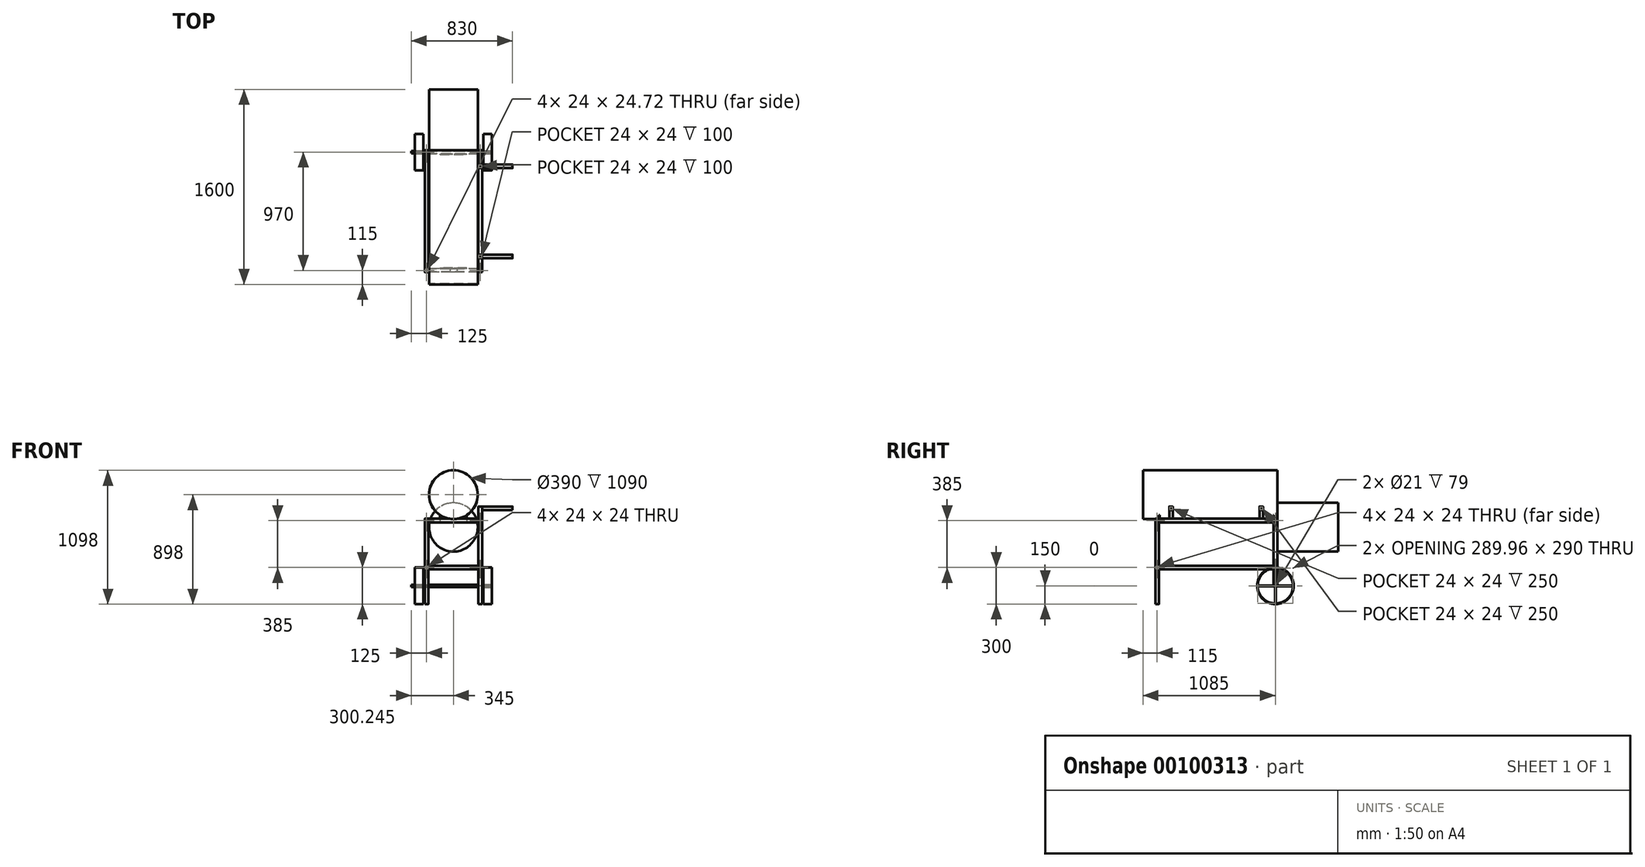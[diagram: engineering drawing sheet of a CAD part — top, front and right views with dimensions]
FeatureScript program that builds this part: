
annotation { "Feature Type Name" : "Feature", "Feature Type Description" : "" }
export const myFeature = defineFeature(function(context is Context, id is Id, definition is map)
    precondition{}
    {
        {
            var Q0;
            Q0=qCreatedBy(makeId("Front.planeOp"),FACE);
            var sketch = newSketch(context, id + "F0", { "sketchPlane" : qUnion([Q0])});
            skLineSegment(sketch, "E0.bottom", {"start": v(15, -350) * mm, "end": v(-15, -350) * mm});
            skLineSegment(sketch, "E0.top", {"start": v(15, 350) * mm, "end": v(-15, 350) * mm});
            skLineSegment(sketch, "E0.left", {"start": v(15, -350) * mm, "end": v(15, 350) * mm});
            skLineSegment(sketch, "E0.right", {"start": v(-15, -350) * mm, "end": v(-15, 350) * mm});
            skPoint(sketch, "E0.middle", {"position": v(0, 0) * mm});
            skSolve(sketch);
        }
        {
            var Q0;
            Q0=makeQuery(id+"F0.imprint","IMPRINT",FACE,{"disambiguationData":[TD([[makeQuery(id+"F0.imprint","IMPRINT",EDGE,{"derivedFrom":sQuery(id+"F0.wireOp",EDGE,"E0.bottom")}),-1.0]])]});
            extrude(context, id + "F1", {"entities" : qUnion([Q0]), "endBound" : BoundingType.SYMMETRIC, "oppositeDirection" : true, "depth" : 30 * mm});
        }
        {
            var Q0;
            Q0=makeQuery(id+"F1.opExtrude","SWEPT_FACE",FACE,{"disambiguationData":[OSD([sQuery(id+"F0.wireOp",EDGE,"E0.bottom")])]});
            var sketch = newSketch(context, id + "F2", { "sketchPlane" : qUnion([Q0])});
            skLineSegment(sketch, "E1.bottom", {"start": v(12, -12.36) * mm, "end": v(-12, -12.36) * mm});
            skLineSegment(sketch, "E1.top", {"start": v(12, 12.36) * mm, "end": v(-12, 12.36) * mm});
            skLineSegment(sketch, "E1.left", {"start": v(12, -12.36) * mm, "end": v(12, 12.36) * mm});
            skLineSegment(sketch, "E1.right", {"start": v(-12, -12.36) * mm, "end": v(-12, 12.36) * mm});
            skPoint(sketch, "E1.middle", {"position": v(0, 0) * mm});
            skSolve(sketch);
        }
        {
            var Q0;
            Q0=makeQuery(id+"F2.imprint","IMPRINT",FACE,{"disambiguationData":[TD([[makeQuery(id+"F2.imprint","IMPRINT",EDGE,{"derivedFrom":sQuery(id+"F2.wireOp",EDGE,"E1.bottom")}),-1.0]])]});
            extrude(context, id + "F3", {"entities" : qUnion([Q0]), "operationType" : NewBodyOperationType.REMOVE, "endBound" : BoundingType.THROUGH_ALL, "oppositeDirection" : true, "depth" : 25 * mm});
        }
        {
            var Q0;
            Q0=makeQuery(id+"F1.opExtrude","CAP_EDGE",EDGE,{"disambiguationData":[OSD([sQuery(id+"F0.wireOp",EDGE,"E0.right")])],"isStart":true});
            fillet(context, id + "F4", {"entities" : qUnion([Q0]), "radius" : 2 * mm, "tangentPropagation" : true, "allowEdgeOverflow" : false});
        }
        {
            var Q0;
            Q0=makeQuery(id+"F1.opExtrude","CAP_EDGE",EDGE,{"disambiguationData":[OSD([sQuery(id+"F0.wireOp",EDGE,"E0.left")])],"isStart":true});
            var Q1;
            Q1=makeQuery(id+"F1.opExtrude","CAP_EDGE",EDGE,{"disambiguationData":[OSD([sQuery(id+"F0.wireOp",EDGE,"E0.left")])],"isStart":false});
            var Q2;
            Q2=makeQuery(id+"F1.opExtrude","CAP_EDGE",EDGE,{"disambiguationData":[OSD([sQuery(id+"F0.wireOp",EDGE,"E0.right")])],"isStart":false});
            fillet(context, id + "F5", {"entities" : qUnion([Q0, Q1, Q2]), "radius" : 2 * mm, "tangentPropagation" : true, "allowEdgeOverflow" : false});
        }
        {
            var Q0;
            Q0=makeQuery(id+"F1.opExtrude","SWEPT_BODY",BODY,{"disambiguationData":[OSD([sQuery(id+"F0.wireOp",EDGE,"E0.bottom"),sQuery(id+"F0.wireOp",EDGE,"E0.top"),sQuery(id+"F0.wireOp",EDGE,"E0.left"),sQuery(id+"F0.wireOp",EDGE,"E0.right")])]});
            transform(context, id + "F6", {"entities" : qUnion([Q0]), "transformType" : TransformType.TRANSLATION_3D, "dx" : 470 * mm, "dy" : 0 * mm, "dz" : 0 * mm, "makeCopy" : true});
        }
        {
            var Q0;
            Q0=makeQuery(id+"F1.opExtrude","SWEPT_BODY",BODY,{"disambiguationData":[OSD([sQuery(id+"F0.wireOp",EDGE,"E0.bottom"),sQuery(id+"F0.wireOp",EDGE,"E0.top"),sQuery(id+"F0.wireOp",EDGE,"E0.left"),sQuery(id+"F0.wireOp",EDGE,"E0.right")])]});
            var Q1;
            Q1=makeQuery(id+"F6.opPattern","COPY",BODY,{"derivedFrom":makeQuery(id+"F1.opExtrude","SWEPT_BODY",BODY,{"disambiguationData":[OSD([sQuery(id+"F0.wireOp",EDGE,"E0.bottom"),sQuery(id+"F0.wireOp",EDGE,"E0.top"),sQuery(id+"F0.wireOp",EDGE,"E0.left"),sQuery(id+"F0.wireOp",EDGE,"E0.right")])]}),"instanceName":"1"});
            transform(context, id + "F7", {"entities" : qUnion([Q0, Q1]), "transformType" : TransformType.TRANSLATION_3D, "dx" : 0 * mm, "dy" : 970 * mm, "dz" : 0 * mm, "makeCopy" : true});
        }
        {
            var Q0;
            Q0=makeQuery(id+"F7.opPattern","COPY",BODY,{"derivedFrom":makeQuery(id+"F6.opPattern","COPY",BODY,{"derivedFrom":makeQuery(id+"F1.opExtrude","SWEPT_BODY",BODY,{"disambiguationData":[OSD([sQuery(id+"F0.wireOp",EDGE,"E0.bottom"),sQuery(id+"F0.wireOp",EDGE,"E0.top"),sQuery(id+"F0.wireOp",EDGE,"E0.left"),sQuery(id+"F0.wireOp",EDGE,"E0.right")])]}),"instanceName":"1"}),"instanceName":"1"});
            var Q1;
            Q1=makeQuery(id+"F6.opPattern","COPY",BODY,{"derivedFrom":makeQuery(id+"F1.opExtrude","SWEPT_BODY",BODY,{"disambiguationData":[OSD([sQuery(id+"F0.wireOp",EDGE,"E0.bottom"),sQuery(id+"F0.wireOp",EDGE,"E0.top"),sQuery(id+"F0.wireOp",EDGE,"E0.left"),sQuery(id+"F0.wireOp",EDGE,"E0.right")])]}),"instanceName":"1"});
            transform(context, id + "F8", {"entities" : qUnion([Q0, Q1]), "transformType" : TransformType.TRANSLATION_3D, "dx" : -60 * mm, "dy" : 0 * mm, "dz" : 0 * mm, "makeCopy" : false});
        }
        {
            var Q0;
            Q0=makeQuery(id+"F7.opPattern","COPY",BODY,{"derivedFrom":makeQuery(id+"F6.opPattern","COPY",BODY,{"derivedFrom":makeQuery(id+"F1.opExtrude","SWEPT_BODY",BODY,{"disambiguationData":[OSD([sQuery(id+"F0.wireOp",EDGE,"E0.bottom"),sQuery(id+"F0.wireOp",EDGE,"E0.top"),sQuery(id+"F0.wireOp",EDGE,"E0.left"),sQuery(id+"F0.wireOp",EDGE,"E0.right")])]}),"instanceName":"1"}),"instanceName":"1"});
            var Q1;
            Q1=makeQuery(id+"F7.opPattern","COPY",BODY,{"derivedFrom":makeQuery(id+"F1.opExtrude","SWEPT_BODY",BODY,{"disambiguationData":[OSD([sQuery(id+"F0.wireOp",EDGE,"E0.bottom"),sQuery(id+"F0.wireOp",EDGE,"E0.top"),sQuery(id+"F0.wireOp",EDGE,"E0.left"),sQuery(id+"F0.wireOp",EDGE,"E0.right")])]}),"instanceName":"1"});
            transform(context, id + "F9", {"entities" : qUnion([Q0, Q1]), "transformType" : TransformType.TRANSLATION_3D, "dx" : 0 * mm, "dy" : -60 * mm, "dz" : 0 * mm, "makeCopy" : false});
        }
        {
            var Q0;
            Q0=makeQuery(id+"F7.opPattern","COPY",FACE,{"derivedFrom":makeQuery(id+"F6.opPattern","COPY",FACE,{"derivedFrom":makeQuery(id+"F1.opExtrude","SWEPT_FACE",FACE,{"disambiguationData":[OSD([sQuery(id+"F0.wireOp",EDGE,"E0.left")])]}),"instanceName":"1"}),"instanceName":"1"});
            var sketch = newSketch(context, id + "F10", { "sketchPlane" : qUnion([Q0])});
            skLineSegment(sketch, "E2.bottom", {"start": v(927.5, -500) * mm, "end": v(892.5, -500) * mm});
            skLineSegment(sketch, "E2.top", {"start": v(927.5, -200) * mm, "end": v(892.5, -200) * mm});
            skLineSegment(sketch, "E2.left", {"start": v(927.5, -350) * mm, "end": v(927.5, -200) * mm});
            skLineSegment(sketch, "E2.right", {"start": v(892.5, -350) * mm, "end": v(892.5, -200) * mm});
            skPoint(sketch, "E2.middle", {"position": v(910, -350) * mm});
            skLineSegment(sketch, "E3", {"start": v(927.5, -350) * mm, "end": v(892.5, -350) * mm});
            skSolve(sketch);
        }
        {
            var Q0;
            {var subQ0=sQuery(id+"F10.wireOp",EDGE,"E2.top");var subQ1=sQuery(id+"F0.wireOp",EDGE,"E0.left");var subQ2=makeQuery(id+"F1.opExtrude","SWEPT_FACE",FACE,{"disambiguationData":[OSD([subQ1])]});var subQ3=makeQuery(id+"F7.opPattern","COPY",EDGE,{"derivedFrom":makeQuery(id+"F6.opPattern","COPY",EDGE,{"derivedFrom":makeQuery(id+"F5.opFillet","BLEND_EDGE",EDGE,{"blendedFrom":[makeQuery(id+"F1.opExtrude","CAP_EDGE",EDGE,{"disambiguationData":[OSD([subQ1])],"isStart":false}),subQ2],"blendedInto":[subQ2]}),"instanceName":"1"}),"instanceName":"1"});var subQ4=makeQuery(id+"F10.imprint","INTERSECT",VERTEX,{"derivedFrom":[subQ3,subQ0]});Q0=makeQuery(id+"F10.imprint","IMPRINT",FACE,{"disambiguationData":[TD([[makeQuery(id+"F10.imprint","IMPRINT",EDGE,{"disambiguationData":[TD([[subQ4,-1.0]])],"derivedFrom":subQ0}),1.0]])]});}
            var Q1;
            {var subQ0=sQuery(id+"F10.wireOp",EDGE,"E2.left");Q1=makeQuery(id+"F10.imprint","IMPRINT",FACE,{"disambiguationData":[TD([[makeQuery(id+"F10.imprint","IMPRINT",EDGE,{"derivedFrom":subQ0}),1.0]])]});}
            var Q2;
            {var subQ0=sQuery(id+"F10.wireOp",EDGE,"E2.right");Q2=makeQuery(id+"F10.imprint","IMPRINT",FACE,{"disambiguationData":[TD([[makeQuery(id+"F10.imprint","IMPRINT",EDGE,{"derivedFrom":subQ0}),-1.0]])]});}
            extrude(context, id + "F11", {"entities" : qUnion([Q0, Q1, Q2]), "operationType" : NewBodyOperationType.REMOVE, "endBound" : BoundingType.THROUGH_ALL, "oppositeDirection" : true, "depth" : 25 * mm});
        }
        {
            var Q0;
            Q0=makeQuery(id+"F7.opPattern","COPY",FACE,{"derivedFrom":makeQuery(id+"F1.opExtrude","SWEPT_FACE",FACE,{"disambiguationData":[OSD([sQuery(id+"F0.wireOp",EDGE,"E0.right")])]}),"instanceName":"1"});
            var sketch = newSketch(context, id + "F12", { "sketchPlane" : qUnion([Q0])});
            skLineSegment(sketch, "E4.bottom", {"start": v(-892.5, -500) * mm, "end": v(-927.5, -500) * mm});
            skLineSegment(sketch, "E4.top", {"start": v(-892.5, -200) * mm, "end": v(-927.5, -200) * mm});
            skLineSegment(sketch, "E4.left", {"start": v(-892.5, -350) * mm, "end": v(-892.5, -200) * mm});
            skLineSegment(sketch, "E4.right", {"start": v(-927.5, -350) * mm, "end": v(-927.5, -200) * mm});
            skPoint(sketch, "E4.middle", {"position": v(-910, -350) * mm});
            skLineSegment(sketch, "E5", {"start": v(-892.5, -350) * mm, "end": v(-927.5, -350) * mm});
            skSolve(sketch);
        }
        {
            var Q0;
            {var subQ0=sQuery(id+"F12.wireOp",EDGE,"E4.right");Q0=makeQuery(id+"F12.imprint","IMPRINT",FACE,{"disambiguationData":[TD([[makeQuery(id+"F12.imprint","IMPRINT",EDGE,{"derivedFrom":subQ0}),-1.0]])]});}
            var Q1;
            {var subQ0=sQuery(id+"F12.wireOp",EDGE,"E4.top");var subQ1=sQuery(id+"F0.wireOp",EDGE,"E0.right");var subQ2=makeQuery(id+"F1.opExtrude","SWEPT_FACE",FACE,{"disambiguationData":[OSD([subQ1])]});var subQ3=makeQuery(id+"F7.opPattern","COPY",EDGE,{"derivedFrom":makeQuery(id+"F4.opFillet","BLEND_EDGE",EDGE,{"blendedFrom":[makeQuery(id+"F1.opExtrude","CAP_EDGE",EDGE,{"disambiguationData":[OSD([subQ1])],"isStart":true}),subQ2],"blendedInto":[subQ2]}),"instanceName":"1"});var subQ4=makeQuery(id+"F12.imprint","INTERSECT",VERTEX,{"derivedFrom":[subQ3,subQ0]});Q1=makeQuery(id+"F12.imprint","IMPRINT",FACE,{"disambiguationData":[TD([[makeQuery(id+"F12.imprint","IMPRINT",EDGE,{"disambiguationData":[TD([[subQ4,-1.0]])],"derivedFrom":subQ0}),1.0]])]});}
            var Q2;
            {var subQ0=sQuery(id+"F12.wireOp",EDGE,"E4.left");Q2=makeQuery(id+"F12.imprint","IMPRINT",FACE,{"disambiguationData":[TD([[makeQuery(id+"F12.imprint","IMPRINT",EDGE,{"derivedFrom":subQ0}),1.0]])]});}
            extrude(context, id + "F13", {"entities" : qUnion([Q0, Q1, Q2]), "operationType" : NewBodyOperationType.REMOVE, "endBound" : BoundingType.THROUGH_ALL, "oppositeDirection" : true, "depth" : 25 * mm});
        }
        {
            var Q0;
            Q0=makeQuery(id+"F7.opPattern","COPY",FACE,{"derivedFrom":makeQuery(id+"F6.opPattern","COPY",FACE,{"derivedFrom":makeQuery(id+"F1.opExtrude","SWEPT_FACE",FACE,{"disambiguationData":[OSD([sQuery(id+"F0.wireOp",EDGE,"E0.left")])]}),"instanceName":"1"}),"instanceName":"1"});
            var sketch = newSketch(context, id + "F14", { "sketchPlane" : qUnion([Q0])});
            skCircle(sketch, "E6", {"center": v(910, -200) * mm, "radius": 10 * mm});
            skSolve(sketch);
        }
        {
            var Q0;
            {var subQ0=sQuery(id+"F14.wireOp",EDGE,"E6");var subQ1=makeQuery(id+"F11.boolean.opBoolean","COPY",EDGE,{"derivedFrom":makeQuery(id+"F11.opExtrude","CAP_EDGE",EDGE,{"disambiguationData":[OSD([sQuery(id+"F10.wireOp",EDGE,"E2.top")])],"isStart":true})});var subQ2=makeQuery(id+"F14.imprint","INTERSECT",VERTEX,{"disambiguationData":[OD(0.0)],"derivedFrom":[subQ1,subQ0]});Q0=makeQuery(id+"F14.imprint","IMPRINT",FACE,{"disambiguationData":[TD([[makeQuery(id+"F14.imprint","IMPRINT",EDGE,{"disambiguationData":[TD([[subQ2,-1.0]])],"derivedFrom":subQ0}),1.0]])]});}
            var Q1;
            {var subQ0=sQuery(id+"F14.wireOp",EDGE,"E6");var subQ1=makeQuery(id+"F11.boolean.opBoolean","COPY",EDGE,{"derivedFrom":makeQuery(id+"F11.opExtrude","CAP_EDGE",EDGE,{"disambiguationData":[OSD([sQuery(id+"F10.wireOp",EDGE,"E2.top")])],"isStart":true})});var subQ2=makeQuery(id+"F14.imprint","INTERSECT",VERTEX,{"disambiguationData":[OD(0.0)],"derivedFrom":[subQ1,subQ0]});Q1=makeQuery(id+"F14.imprint","IMPRINT",FACE,{"disambiguationData":[TD([[makeQuery(id+"F14.imprint","IMPRINT",EDGE,{"disambiguationData":[TD([[subQ2,1.0]])],"derivedFrom":subQ0}),1.0]])]});}
            extrude(context, id + "F15", {"entities" : qUnion([Q0, Q1]), "operationType" : NewBodyOperationType.ADD, "depth" : 50 * mm});
        }
        {
            var Q0;
            Q0=makeQuery(id+"F15.opExtrude","CAP_FACE",FACE,{"disambiguationData":[OSD([sQuery(id+"F14.wireOp",EDGE,"E6")])],"isStart":true});
            extrude(context, id + "F16", {"entities" : qUnion([Q0]), "depth" : 490 * mm});
        }
        {
            var Q0;
            Q0=makeQuery(id+"F16.opExtrude","SWEPT_BODY",BODY,{"disambiguationData":[OSD([sQuery(id+"F14.wireOp",EDGE,"E6")])]});
            var Q1;
            Q1=makeQuery(id+"F16.opExtrude","SWEPT_FACE",FACE,{"disambiguationData":[OSD([sQuery(id+"F10.wireOp",EDGE,"E2.top")])]});
            mirror(context, id + "F17", {"entities" : qUnion([Q0]), "mirrorPlane" : qUnion([Q1])});
        }
        {
            var Q0;
            Q0=makeQuery(id+"F17.opPattern","COPY",BODY,{"derivedFrom":makeQuery(id+"F16.opExtrude","SWEPT_BODY",BODY,{"disambiguationData":[OSD([sQuery(id+"F14.wireOp",EDGE,"E6")])]}),"instanceName":"1"});
            var Q1;
            Q1=makeQuery(id+"F16.opExtrude","SWEPT_BODY",BODY,{"disambiguationData":[OSD([sQuery(id+"F14.wireOp",EDGE,"E6")])]});
            booleanBodies(context, id + "F18", {"operationType" : BooleanOperationType.UNION, "tools" : qUnion([Q0, Q1])});
        }
        {
            var Q0;
            Q0=makeQuery(id+"F15.opExtrude","CAP_FACE",FACE,{"disambiguationData":[OSD([sQuery(id+"F14.wireOp",EDGE,"E6")])],"isStart":false});
            var sketch = newSketch(context, id + "F19", { "sketchPlane" : qUnion([Q0])});
            skCircle(sketch, "E7", {"center": v(910, -200) * mm, "radius": 10.4 * mm});
            skSolve(sketch);
        }
        {
            var Q0;
            Q0=makeQuery(id+"F19.imprint","IMPRINT",FACE,{"disambiguationData":[TD([[makeQuery(id+"F19.imprint","IMPRINT",EDGE,{"derivedFrom":makeQuery(id+"F15.opExtrude","CAP_EDGE",EDGE,{"disambiguationData":[OSD([sQuery(id+"F14.wireOp",EDGE,"E6")])],"isStart":false})}),1.0]])]});
            extrude(context, id + "F20", {"entities" : qUnion([Q0]), "operationType" : NewBodyOperationType.ADD, "depth" : 30 * mm});
        }
        {
            var Q0;
            {var subQ0=makeQuery(id+"F16.opExtrude","CAP_FACE",FACE,{"disambiguationData":[OSD([sQuery(id+"F14.wireOp",EDGE,"E6")])],"isStart":false});Q0=makeQuery(id+"F18.opBoolean","MERGE",FACE,{"derivedFrom":[subQ0,makeQuery(id+"F17.opPattern","COPY",FACE,{"derivedFrom":subQ0,"instanceName":"1"})]});}
            extrude(context, id + "F21", {"entities" : qUnion([Q0]), "operationType" : NewBodyOperationType.ADD, "depth" : 30 * mm});
        }
        {
            var Q0;
            Q0=makeQuery(id+"F20.opExtrude","CAP_FACE",FACE,{"disambiguationData":[OSD([sQuery(id+"F14.wireOp",EDGE,"E6")])],"isStart":false});
            var sketch = newSketch(context, id + "F22", { "sketchPlane" : qUnion([Q0])});
            skCircle(sketch, "E8", {"center": v(910, -200) * mm, "radius": 10.5 * mm});
            skCircle(sketch, "E9", {"center": v(910, -200) * mm, "radius": 12 * mm});
            skSolve(sketch);
        }
        {
            var Q0;
            Q0=makeQuery(id+"F22.imprint","IMPRINT",FACE,{"disambiguationData":[TD([[makeQuery(id+"F22.imprint","IMPRINT",EDGE,{"derivedFrom":sQuery(id+"F22.wireOp",EDGE,"E8")}),-1.0]])]});
            extrude(context, id + "F23", {"entities" : qUnion([Q0]), "oppositeDirection" : true, "depth" : 79 * mm});
        }
        {
            var Q0;
            Q0=makeQuery(id+"F20.opExtrude","CAP_FACE",FACE,{"disambiguationData":[OSD([sQuery(id+"F14.wireOp",EDGE,"E6")])],"isStart":false});
            var sketch = newSketch(context, id + "F24", { "sketchPlane" : qUnion([Q0])});
            skCircle(sketch, "E10", {"center": v(910, -200) * mm, "radius": 150 * mm});
            skCircle(sketch, "E11", {"center": v(910, -200) * mm, "radius": 145 * mm});
            skLineSegment(sketch, "E12.bottom", {"start": v(912.5, -344.98) * mm, "end": v(907.5, -344.98) * mm});
            skLineSegment(sketch, "E12.top", {"start": v(912.5, -55.02) * mm, "end": v(907.5, -55.02) * mm});
            skLineSegment(sketch, "E12.left", {"start": v(912.5, -344.98) * mm, "end": v(912.5, -211.74) * mm});
            skLineSegment(sketch, "E12.right", {"start": v(907.5, -344.98) * mm, "end": v(907.5, -211.74) * mm});
            skLineSegment(sketch, "E13.bottom", {"start": v(1054.98, -202.5) * mm, "end": v(921.74, -202.5) * mm});
            skLineSegment(sketch, "E13.top", {"start": v(1054.98, -197.5) * mm, "end": v(921.74, -197.5) * mm});
            skPoint(sketch, "E13.left.end.orphan", {"position": v(1076.87, -197.5) * mm});
            skPoint(sketch, "E13.left.start.orphan", {"position": v(1076.87, -202.5) * mm});
            skPoint(sketch, "E13.right.end.orphan", {"position": v(743.13, -197.5) * mm});
            skPoint(sketch, "E13.right.start.orphan", {"position": v(743.13, -202.5) * mm});
            skCircle(sketch, "E14", {"center": v(910, -200) * mm, "radius": 12 * mm});
            skLineSegment(sketch, "E15.trimOffspring", {"start": v(898.26, -197.5) * mm, "end": v(765.02, -197.5) * mm});
            skLineSegment(sketch, "E16.trimOffspring", {"start": v(898.26, -202.5) * mm, "end": v(765.02, -202.5) * mm});
            skLineSegment(sketch, "E17.trimOffspring", {"start": v(907.5, -188.26) * mm, "end": v(907.5, -55.02) * mm});
            skLineSegment(sketch, "E18.trimOffspring", {"start": v(912.5, -188.26) * mm, "end": v(912.5, -55.02) * mm});
            skSolve(sketch);
        }
        {
            var Q0;
            Q0=makeQuery(id+"F24.imprint","IMPRINT",FACE,{"disambiguationData":[TD([[makeQuery(id+"F24.imprint","IMPRINT",EDGE,{"derivedFrom":sQuery(id+"F24.wireOp",EDGE,"E10")}),1.0]])]});
            var Q1;
            {var subQ0=sQuery(id+"F24.wireOp",EDGE,"E15.trimOffspring");Q1=makeQuery(id+"F24.imprint","IMPRINT",FACE,{"disambiguationData":[TD([[makeQuery(id+"F24.imprint","IMPRINT",EDGE,{"derivedFrom":subQ0}),1.0]])]});}
            var Q2;
            Q2=makeQuery(id+"F24.imprint","IMPRINT",FACE,{"disambiguationData":[TD([[makeQuery(id+"F24.imprint","IMPRINT",EDGE,{"derivedFrom":sQuery(id+"F24.wireOp",EDGE,"E12.bottom")}),-1.0]])]});
            var Q3;
            Q3=makeQuery(id+"F24.imprint","IMPRINT",FACE,{"disambiguationData":[TD([[makeQuery(id+"F24.imprint","IMPRINT",EDGE,{"derivedFrom":sQuery(id+"F24.wireOp",EDGE,"E12.top")}),1.0]])]});
            var Q4;
            {var subQ0=sQuery(id+"F24.wireOp",EDGE,"E13.bottom");Q4=makeQuery(id+"F24.imprint","IMPRINT",FACE,{"disambiguationData":[TD([[makeQuery(id+"F24.imprint","IMPRINT",EDGE,{"derivedFrom":subQ0}),-1.0]])]});}
            extrude(context, id + "F25", {"entities" : qUnion([Q0, Q1, Q2, Q3, Q4]), "oppositeDirection" : true, "depth" : 70 * mm});
        }
        {
            var Q0;
            Q0=makeQuery(id+"F25.opExtrude","SWEPT_BODY",BODY,{"disambiguationData":[OSD([sQuery(id+"F24.wireOp",EDGE,"E10"),sQuery(id+"F24.wireOp",EDGE,"E11"),sQuery(id+"F24.wireOp",EDGE,"E13.bottom"),sQuery(id+"F24.wireOp",EDGE,"E13.top"),sQuery(id+"F24.wireOp",EDGE,"E14"),sQuery(id+"F24.wireOp",EDGE,"E15.trimOffspring"),sQuery(id+"F24.wireOp",EDGE,"E16.trimOffspring")])]});
            var Q1;
            Q1=makeQuery(id+"F25.opExtrude","SWEPT_BODY",BODY,{"disambiguationData":[OSD([sQuery(id+"F24.wireOp",EDGE,"E12.bottom"),sQuery(id+"F24.wireOp",EDGE,"E12.left"),sQuery(id+"F24.wireOp",EDGE,"E12.right"),sQuery(id+"F24.wireOp",EDGE,"E14")])]});
            var Q2;
            Q2=makeQuery(id+"F25.opExtrude","SWEPT_BODY",BODY,{"disambiguationData":[OSD([sQuery(id+"F24.wireOp",EDGE,"E12.top"),sQuery(id+"F24.wireOp",EDGE,"E14"),sQuery(id+"F24.wireOp",EDGE,"E17.trimOffspring"),sQuery(id+"F24.wireOp",EDGE,"E18.trimOffspring")])]});
            transform(context, id + "F26", {"entities" : qUnion([Q0, Q1, Q2]), "transformType" : TransformType.TRANSLATION_3D, "dx" : -530 * mm, "dy" : 0 * mm, "dz" : 0 * mm, "makeCopy" : true});
        }
        {
            var Q0;
            Q0=makeQuery(id+"F23.opExtrude","SWEPT_BODY",BODY,{"disambiguationData":[OSD([sQuery(id+"F22.wireOp",EDGE,"E8"),sQuery(id+"F22.wireOp",EDGE,"E9")])]});
            transform(context, id + "F27", {"entities" : qUnion([Q0]), "transformType" : TransformType.TRANSLATION_3D, "dx" : -521 * mm, "dy" : 0 * mm, "dz" : 0 * mm, "makeCopy" : true});
        }
        {
            var Q0;
            Q0=makeQuery(id+"F7.opPattern","COPY",FACE,{"derivedFrom":makeQuery(id+"F1.opExtrude","CAP_FACE",FACE,{"disambiguationData":[OSD([sQuery(id+"F0.wireOp",EDGE,"E0.bottom"),sQuery(id+"F0.wireOp",EDGE,"E0.top"),sQuery(id+"F0.wireOp",EDGE,"E0.left"),sQuery(id+"F0.wireOp",EDGE,"E0.right")])],"isStart":true}),"instanceName":"1"});
            var sketch = newSketch(context, id + "F28", { "sketchPlane" : qUnion([Q0])});
            skLineSegment(sketch, "E19.bottom", {"start": v(13, -170) * mm, "end": v(-13, -170) * mm});
            skLineSegment(sketch, "E19.left", {"start": v(15, -172) * mm, "end": v(15, -198) * mm});
            skLineSegment(sketch, "E19.right", {"start": v(-15, -172) * mm, "end": v(-15, -198) * mm});
            skPoint(sketch, "E19.middle", {"position": v(0, -200) * mm});
            skLineSegment(sketch, "E20", {"start": v(0, -200) * mm, "end": v(-15, -200) * mm});
            skLineSegment(sketch, "E21", {"start": v(-13, -200) * mm, "end": v(13, -200) * mm});
            skPoint(sketch, "E19.top.start.orphan", {"position": v(15, -230) * mm});
            skPoint(sketch, "E22.orphan", {"position": v(-15, -230) * mm});
            skPoint(sketch, "E23.visualSharp", {"position": v(15, -170) * mm});
            skArc(sketch, "E23.filletArc", {"start": v(15, -172) * mm, "mid": v(14.41, -170.59) * mm, "end": v(13, -170) * mm});
            skPoint(sketch, "E24.visualSharp", {"position": v(15, -200) * mm});
            skArc(sketch, "E24.filletArc", {"start": v(13, -200) * mm, "mid": v(14.41, -199.41) * mm, "end": v(15, -198) * mm});
            skPoint(sketch, "E25.visualSharp", {"position": v(-15, -200) * mm});
            skArc(sketch, "E25.filletArc", {"start": v(-15, -198) * mm, "mid": v(-14.41, -199.41) * mm, "end": v(-13, -200) * mm});
            skPoint(sketch, "E26.visualSharp", {"position": v(-15, -170) * mm});
            skArc(sketch, "E26.filletArc", {"start": v(-13, -170) * mm, "mid": v(-14.41, -170.59) * mm, "end": v(-15, -172) * mm});
            skSolve(sketch);
        }
        {
            var Q0;
            Q0=makeQuery(id+"F1.opExtrude","SWEPT_BODY",BODY,{"disambiguationData":[OSD([sQuery(id+"F0.wireOp",EDGE,"E0.bottom"),sQuery(id+"F0.wireOp",EDGE,"E0.top"),sQuery(id+"F0.wireOp",EDGE,"E0.left"),sQuery(id+"F0.wireOp",EDGE,"E0.right")])]});
            var Q1;
            Q1=makeQuery(id+"F6.opPattern","COPY",BODY,{"derivedFrom":makeQuery(id+"F1.opExtrude","SWEPT_BODY",BODY,{"disambiguationData":[OSD([sQuery(id+"F0.wireOp",EDGE,"E0.bottom"),sQuery(id+"F0.wireOp",EDGE,"E0.top"),sQuery(id+"F0.wireOp",EDGE,"E0.left"),sQuery(id+"F0.wireOp",EDGE,"E0.right")])]}),"instanceName":"1"});
            var Q2;
            Q2=makeQuery(id+"FpJCvMGEq1ND3XV_5.opExtrude","SWEPT_BODY",BODY,{"disambiguationData":[OSD([sQuery(id+"F28.wireOp",EDGE,"E19.bottom"),sQuery(id+"F28.wireOp",EDGE,"E19.left"),sQuery(id+"F28.wireOp",EDGE,"E19.right"),sQuery(id+"F28.wireOp",EDGE,"E21"),sQuery(id+"F28.wireOp",EDGE,"E23.filletArc"),sQuery(id+"F28.wireOp",EDGE,"E24.filletArc"),sQuery(id+"F28.wireOp",EDGE,"E25.filletArc"),sQuery(id+"F28.wireOp",EDGE,"E26.filletArc")])]});
            transform(context, id + "F29", {"entities" : qUnion([Q0, Q1, Q2]), "transformType" : TransformType.TRANSLATION_3D, "dx" : 0 * mm, "dy" : -60 * mm, "dz" : 0 * mm, "makeCopy" : false});
        }
        {
            var Q0;
            Q0=makeQuery(id+"F6.opPattern","COPY",BODY,{"derivedFrom":makeQuery(id+"F1.opExtrude","SWEPT_BODY",BODY,{"disambiguationData":[OSD([sQuery(id+"F0.wireOp",EDGE,"E0.bottom"),sQuery(id+"F0.wireOp",EDGE,"E0.top"),sQuery(id+"F0.wireOp",EDGE,"E0.left"),sQuery(id+"F0.wireOp",EDGE,"E0.right")])]}),"instanceName":"1"});
            var Q1;
            Q1=makeQuery(id+"F23.opExtrude","SWEPT_BODY",BODY,{"disambiguationData":[OSD([sQuery(id+"F22.wireOp",EDGE,"E8"),sQuery(id+"F22.wireOp",EDGE,"E9")])]});
            var Q2;
            Q2=makeQuery(id+"F25.opExtrude","SWEPT_BODY",BODY,{"disambiguationData":[OSD([sQuery(id+"F24.wireOp",EDGE,"E10"),sQuery(id+"F24.wireOp",EDGE,"E11"),sQuery(id+"F24.wireOp",EDGE,"E13.bottom"),sQuery(id+"F24.wireOp",EDGE,"E13.top"),sQuery(id+"F24.wireOp",EDGE,"E14"),sQuery(id+"F24.wireOp",EDGE,"E15.trimOffspring"),sQuery(id+"F24.wireOp",EDGE,"E16.trimOffspring")])]});
            var Q3;
            Q3=makeQuery(id+"F25.opExtrude","SWEPT_BODY",BODY,{"disambiguationData":[OSD([sQuery(id+"F24.wireOp",EDGE,"E12.top"),sQuery(id+"F24.wireOp",EDGE,"E14"),sQuery(id+"F24.wireOp",EDGE,"E17.trimOffspring"),sQuery(id+"F24.wireOp",EDGE,"E18.trimOffspring")])]});
            var Q4;
            Q4=makeQuery(id+"F25.opExtrude","SWEPT_BODY",BODY,{"disambiguationData":[OSD([sQuery(id+"F24.wireOp",EDGE,"E12.bottom"),sQuery(id+"F24.wireOp",EDGE,"E12.left"),sQuery(id+"F24.wireOp",EDGE,"E12.right"),sQuery(id+"F24.wireOp",EDGE,"E14")])]});
            var Q5;
            Q5=makeQuery(id+"F7.opPattern","COPY",BODY,{"derivedFrom":makeQuery(id+"F6.opPattern","COPY",BODY,{"derivedFrom":makeQuery(id+"F1.opExtrude","SWEPT_BODY",BODY,{"disambiguationData":[OSD([sQuery(id+"F0.wireOp",EDGE,"E0.bottom"),sQuery(id+"F0.wireOp",EDGE,"E0.top"),sQuery(id+"F0.wireOp",EDGE,"E0.left"),sQuery(id+"F0.wireOp",EDGE,"E0.right")])]}),"instanceName":"1"}),"instanceName":"1"});
            transform(context, id + "F30", {"entities" : qUnion([Q0, Q1, Q2, Q3, Q4, Q5]), "transformType" : TransformType.TRANSLATION_3D, "dx" : 30 * mm, "dy" : 0 * mm, "dz" : 0 * mm, "makeCopy" : false});
        }
        {
            var Q0;
            Q0=makeQuery(id+"F21.opExtrude","CAP_FACE",FACE,{"disambiguationData":[OSD([sQuery(id+"F14.wireOp",EDGE,"E6")])],"isStart":false});
            extrude(context, id + "F31", {"entities" : qUnion([Q0]), "operationType" : NewBodyOperationType.ADD, "depth" : 30 * mm});
        }
        {
            var Q0;
            {var subQ0=sQuery(id+"F28.wireOp",EDGE,"E19.bottom");Q0=makeQuery(id+"F28.imprint","IMPRINT",FACE,{"disambiguationData":[TD([[makeQuery(id+"F28.imprint","IMPRINT",EDGE,{"derivedFrom":subQ0}),1.0]])]});}
            var sketch = newSketch(context, id + "F32", { "sketchPlane" : qUnion([Q0])});
            skLineSegment(sketch, "E27", {"start": v(0, -201.76) * mm, "end": v(0, -51.76) * mm});
            skLineSegment(sketch, "E28.bottom", {"start": v(13, -66.76) * mm, "end": v(-13, -66.76) * mm});
            skLineSegment(sketch, "E28.top", {"start": v(13, -36.76) * mm, "end": v(-13, -36.76) * mm});
            skLineSegment(sketch, "E28.left", {"start": v(15, -64.76) * mm, "end": v(15, -38.76) * mm});
            skLineSegment(sketch, "E28.right", {"start": v(-15, -64.76) * mm, "end": v(-15, -38.76) * mm});
            skPoint(sketch, "E28.middle", {"position": v(0, -51.76) * mm});
            skLineSegment(sketch, "E29.bottom", {"start": v(12, -63.76) * mm, "end": v(-12, -63.76) * mm});
            skLineSegment(sketch, "E29.top", {"start": v(12, -39.76) * mm, "end": v(-12, -39.76) * mm});
            skLineSegment(sketch, "E29.left", {"start": v(12, -63.76) * mm, "end": v(12, -39.76) * mm});
            skLineSegment(sketch, "E29.right", {"start": v(-12, -63.76) * mm, "end": v(-12, -39.76) * mm});
            skPoint(sketch, "E30.visualSharp", {"position": v(15, -36.76) * mm});
            skArc(sketch, "E30.filletArc", {"start": v(15, -38.76) * mm, "mid": v(14.41, -37.34) * mm, "end": v(13, -36.76) * mm});
            skPoint(sketch, "E31.visualSharp", {"position": v(15, -66.76) * mm});
            skArc(sketch, "E31.filletArc", {"start": v(13, -66.76) * mm, "mid": v(14.41, -66.17) * mm, "end": v(15, -64.76) * mm});
            skPoint(sketch, "E32.visualSharp", {"position": v(-15, -66.76) * mm});
            skArc(sketch, "E32.filletArc", {"start": v(-15, -64.76) * mm, "mid": v(-14.41, -66.17) * mm, "end": v(-13, -66.76) * mm});
            skPoint(sketch, "E33.visualSharp", {"position": v(-15, -36.76) * mm});
            skArc(sketch, "E33.filletArc", {"start": v(-13, -36.76) * mm, "mid": v(-14.41, -37.34) * mm, "end": v(-15, -38.76) * mm});
            skSolve(sketch);
        }
        {
            var Q0;
            Q0=makeQuery(id+"F32.imprint","IMPRINT",FACE,{"disambiguationData":[TD([[makeQuery(id+"F32.imprint","IMPRINT",EDGE,{"derivedFrom":sQuery(id+"F32.wireOp",EDGE,"E28.top")}),1.0]])]});
            var Q1;
            Q1=makeQuery(id+"F1.opExtrude","CAP_FACE",FACE,{"disambiguationData":[OSD([sQuery(id+"F0.wireOp",EDGE,"E0.bottom"),sQuery(id+"F0.wireOp",EDGE,"E0.top"),sQuery(id+"F0.wireOp",EDGE,"E0.left"),sQuery(id+"F0.wireOp",EDGE,"E0.right")])],"isStart":false});
            extrude(context, id + "F33", {"entities" : qUnion([Q0]), "endBound" : BoundingType.UP_TO_SURFACE, "endBoundEntityFace" : qUnion([Q1]), "depth" : 25 * mm});
        }
        {
            var Q0;
            Q0=makeQuery(id+"F33.opExtrude","SWEPT_BODY",BODY,{"disambiguationData":[OSD([sQuery(id+"F32.wireOp",EDGE,"E28.bottom"),sQuery(id+"F32.wireOp",EDGE,"E28.top"),sQuery(id+"F32.wireOp",EDGE,"E28.left"),sQuery(id+"F32.wireOp",EDGE,"E28.right"),sQuery(id+"F32.wireOp",EDGE,"E29.bottom"),sQuery(id+"F32.wireOp",EDGE,"E29.top"),sQuery(id+"F32.wireOp",EDGE,"E29.left"),sQuery(id+"F32.wireOp",EDGE,"E29.right"),sQuery(id+"F32.wireOp",EDGE,"E30.filletArc"),sQuery(id+"F32.wireOp",EDGE,"E31.filletArc"),sQuery(id+"F32.wireOp",EDGE,"E32.filletArc"),sQuery(id+"F32.wireOp",EDGE,"E33.filletArc")])]});
            transform(context, id + "F34", {"entities" : qUnion([Q0]), "transformType" : TransformType.TRANSLATION_3D, "dx" : 440 * mm, "dy" : 0 * mm, "dz" : 0 * mm, "makeCopy" : true});
        }
        {
            var Q0;
            Q0=makeQuery(id+"F33.opExtrude","SWEPT_BODY",BODY,{"disambiguationData":[OSD([sQuery(id+"F32.wireOp",EDGE,"E28.bottom"),sQuery(id+"F32.wireOp",EDGE,"E28.top"),sQuery(id+"F32.wireOp",EDGE,"E28.left"),sQuery(id+"F32.wireOp",EDGE,"E28.right"),sQuery(id+"F32.wireOp",EDGE,"E29.bottom"),sQuery(id+"F32.wireOp",EDGE,"E29.top"),sQuery(id+"F32.wireOp",EDGE,"E29.left"),sQuery(id+"F32.wireOp",EDGE,"E29.right"),sQuery(id+"F32.wireOp",EDGE,"E30.filletArc"),sQuery(id+"F32.wireOp",EDGE,"E31.filletArc"),sQuery(id+"F32.wireOp",EDGE,"E32.filletArc"),sQuery(id+"F32.wireOp",EDGE,"E33.filletArc")])]});
            var Q1;
            Q1=makeQuery(id+"F34.opPattern","COPY",BODY,{"derivedFrom":makeQuery(id+"F33.opExtrude","SWEPT_BODY",BODY,{"disambiguationData":[OSD([sQuery(id+"F32.wireOp",EDGE,"E28.bottom"),sQuery(id+"F32.wireOp",EDGE,"E28.top"),sQuery(id+"F32.wireOp",EDGE,"E28.left"),sQuery(id+"F32.wireOp",EDGE,"E28.right"),sQuery(id+"F32.wireOp",EDGE,"E29.bottom"),sQuery(id+"F32.wireOp",EDGE,"E29.top"),sQuery(id+"F32.wireOp",EDGE,"E29.left"),sQuery(id+"F32.wireOp",EDGE,"E29.right"),sQuery(id+"F32.wireOp",EDGE,"E30.filletArc"),sQuery(id+"F32.wireOp",EDGE,"E31.filletArc"),sQuery(id+"F32.wireOp",EDGE,"E32.filletArc"),sQuery(id+"F32.wireOp",EDGE,"E33.filletArc")])]}),"instanceName":"1"});
            transform(context, id + "F35", {"entities" : qUnion([Q0, Q1]), "transformType" : TransformType.TRANSLATION_3D, "dx" : 0 * mm, "dy" : 0 * mm, "dz" : 387 * mm, "makeCopy" : true});
        }
        {
            var Q0;
            Q0=makeQuery(id+"F34.opPattern","COPY",BODY,{"derivedFrom":makeQuery(id+"F33.opExtrude","SWEPT_BODY",BODY,{"disambiguationData":[OSD([sQuery(id+"F32.wireOp",EDGE,"E28.bottom"),sQuery(id+"F32.wireOp",EDGE,"E28.top"),sQuery(id+"F32.wireOp",EDGE,"E28.left"),sQuery(id+"F32.wireOp",EDGE,"E28.right"),sQuery(id+"F32.wireOp",EDGE,"E29.bottom"),sQuery(id+"F32.wireOp",EDGE,"E29.top"),sQuery(id+"F32.wireOp",EDGE,"E29.left"),sQuery(id+"F32.wireOp",EDGE,"E29.right"),sQuery(id+"F32.wireOp",EDGE,"E30.filletArc"),sQuery(id+"F32.wireOp",EDGE,"E31.filletArc"),sQuery(id+"F32.wireOp",EDGE,"E32.filletArc"),sQuery(id+"F32.wireOp",EDGE,"E33.filletArc")])]}),"instanceName":"1"});
            var Q1;
            Q1=makeQuery(id+"F33.opExtrude","SWEPT_BODY",BODY,{"disambiguationData":[OSD([sQuery(id+"F32.wireOp",EDGE,"E28.bottom"),sQuery(id+"F32.wireOp",EDGE,"E28.top"),sQuery(id+"F32.wireOp",EDGE,"E28.left"),sQuery(id+"F32.wireOp",EDGE,"E28.right"),sQuery(id+"F32.wireOp",EDGE,"E29.bottom"),sQuery(id+"F32.wireOp",EDGE,"E29.top"),sQuery(id+"F32.wireOp",EDGE,"E29.left"),sQuery(id+"F32.wireOp",EDGE,"E29.right"),sQuery(id+"F32.wireOp",EDGE,"E30.filletArc"),sQuery(id+"F32.wireOp",EDGE,"E31.filletArc"),sQuery(id+"F32.wireOp",EDGE,"E32.filletArc"),sQuery(id+"F32.wireOp",EDGE,"E33.filletArc")])]});
            transform(context, id + "F36", {"entities" : qUnion([Q0, Q1]), "transformType" : TransformType.TRANSLATION_3D, "dx" : 0 * mm, "dy" : 0 * mm, "dz" : 2 * mm, "makeCopy" : false});
        }
        {
            var Q0;
            Q0=makeQuery(id+"F7.opPattern","COPY",FACE,{"derivedFrom":makeQuery(id+"F1.opExtrude","SWEPT_FACE",FACE,{"disambiguationData":[OSD([sQuery(id+"F0.wireOp",EDGE,"E0.left")])]}),"instanceName":"1"});
            var sketch = newSketch(context, id + "F37", { "sketchPlane" : qUnion([Q0])});
            skLineSegment(sketch, "E34.bottom", {"start": v(923, -65) * mm, "end": v(897, -65) * mm});
            skLineSegment(sketch, "E34.top", {"start": v(923, -35) * mm, "end": v(897, -35) * mm});
            skLineSegment(sketch, "E34.left", {"start": v(925, -63) * mm, "end": v(925, -37) * mm});
            skLineSegment(sketch, "E34.right", {"start": v(895, -63) * mm, "end": v(895, -37) * mm});
            skPoint(sketch, "E34.middle", {"position": v(910, -50) * mm});
            skLineSegment(sketch, "E35.bottom", {"start": v(922, -62) * mm, "end": v(898, -62) * mm});
            skLineSegment(sketch, "E35.top", {"start": v(922, -38) * mm, "end": v(898, -38) * mm});
            skLineSegment(sketch, "E35.left", {"start": v(922, -62) * mm, "end": v(922, -38) * mm});
            skLineSegment(sketch, "E35.right", {"start": v(898, -62) * mm, "end": v(898, -38) * mm});
            skPoint(sketch, "E36.visualSharp", {"position": v(925, -35) * mm});
            skArc(sketch, "E36.filletArc", {"start": v(925, -37) * mm, "mid": v(924.41, -35.59) * mm, "end": v(923, -35) * mm});
            skPoint(sketch, "E37.visualSharp", {"position": v(925, -65) * mm});
            skArc(sketch, "E37.filletArc", {"start": v(923, -65) * mm, "mid": v(924.41, -64.41) * mm, "end": v(925, -63) * mm});
            skPoint(sketch, "E38.visualSharp", {"position": v(895, -65) * mm});
            skArc(sketch, "E38.filletArc", {"start": v(895, -63) * mm, "mid": v(895.59, -64.41) * mm, "end": v(897, -65) * mm});
            skPoint(sketch, "E39.visualSharp", {"position": v(895, -35) * mm});
            skArc(sketch, "E39.filletArc", {"start": v(897, -35) * mm, "mid": v(895.59, -35.59) * mm, "end": v(895, -37) * mm});
            skSolve(sketch);
        }
        {
            var Q0;
            {var subQ0=sQuery(id+"F37.wireOp",EDGE,"E34.bottom");Q0=makeQuery(id+"F37.imprint","IMPRINT",FACE,{"disambiguationData":[TD([[makeQuery(id+"F37.imprint","IMPRINT",EDGE,{"derivedFrom":subQ0}),-1.0]])]});}
            var Q1;
            Q1=makeQuery(id+"F37.imprint","IMPRINT",FACE,{"disambiguationData":[TD([[makeQuery(id+"F37.imprint","IMPRINT",EDGE,{"derivedFrom":sQuery(id+"F37.wireOp",EDGE,"E34.left")}),1.0]])]});
            var Q2;
            Q2=makeQuery(id+"F37.imprint","IMPRINT",FACE,{"disambiguationData":[TD([[makeQuery(id+"F37.imprint","IMPRINT",EDGE,{"derivedFrom":sQuery(id+"F37.wireOp",EDGE,"E34.right")}),-1.0]])]});
            var Q3;
            Q3=makeQuery(id+"F7.opPattern","COPY",FACE,{"derivedFrom":makeQuery(id+"F6.opPattern","COPY",FACE,{"derivedFrom":makeQuery(id+"F1.opExtrude","SWEPT_FACE",FACE,{"disambiguationData":[OSD([sQuery(id+"F0.wireOp",EDGE,"E0.right")])]}),"instanceName":"1"}),"instanceName":"1"});
            extrude(context, id + "F38", {"entities" : qUnion([Q0, Q1, Q2]), "endBound" : BoundingType.UP_TO_SURFACE, "endBoundEntityFace" : qUnion([Q3]), "depth" : 25 * mm});
        }
        {
            var Q0;
            Q0=makeQuery(id+"F38.opExtrude","SWEPT_BODY",BODY,{"disambiguationData":[OSD([sQuery(id+"F37.wireOp",EDGE,"E34.bottom"),sQuery(id+"F37.wireOp",EDGE,"E34.top"),sQuery(id+"F37.wireOp",EDGE,"E34.left"),sQuery(id+"F37.wireOp",EDGE,"E34.right"),sQuery(id+"F37.wireOp",EDGE,"E35.bottom"),sQuery(id+"F37.wireOp",EDGE,"E35.top"),sQuery(id+"F37.wireOp",EDGE,"E35.left"),sQuery(id+"F37.wireOp",EDGE,"E35.right"),sQuery(id+"F37.wireOp",EDGE,"E36.filletArc"),sQuery(id+"F37.wireOp",EDGE,"E37.filletArc"),sQuery(id+"F37.wireOp",EDGE,"E38.filletArc"),sQuery(id+"F37.wireOp",EDGE,"E39.filletArc")])]});
            transform(context, id + "F39", {"entities" : qUnion([Q0]), "transformType" : TransformType.TRANSLATION_3D, "dx" : 0 * mm, "dy" : 0 * mm, "dz" : 385 * mm, "makeCopy" : true});
        }
        {
            var Q0;
            Q0=makeQuery(id+"F38.opExtrude","SWEPT_BODY",BODY,{"disambiguationData":[OSD([sQuery(id+"F37.wireOp",EDGE,"E34.bottom"),sQuery(id+"F37.wireOp",EDGE,"E34.top"),sQuery(id+"F37.wireOp",EDGE,"E34.left"),sQuery(id+"F37.wireOp",EDGE,"E34.right"),sQuery(id+"F37.wireOp",EDGE,"E35.bottom"),sQuery(id+"F37.wireOp",EDGE,"E35.top"),sQuery(id+"F37.wireOp",EDGE,"E35.left"),sQuery(id+"F37.wireOp",EDGE,"E35.right"),sQuery(id+"F37.wireOp",EDGE,"E36.filletArc"),sQuery(id+"F37.wireOp",EDGE,"E37.filletArc"),sQuery(id+"F37.wireOp",EDGE,"E38.filletArc"),sQuery(id+"F37.wireOp",EDGE,"E39.filletArc")])]});
            var Q1;
            Q1=makeQuery(id+"F39.opPattern","COPY",BODY,{"derivedFrom":makeQuery(id+"F38.opExtrude","SWEPT_BODY",BODY,{"disambiguationData":[OSD([sQuery(id+"F37.wireOp",EDGE,"E34.bottom"),sQuery(id+"F37.wireOp",EDGE,"E34.top"),sQuery(id+"F37.wireOp",EDGE,"E34.left"),sQuery(id+"F37.wireOp",EDGE,"E34.right"),sQuery(id+"F37.wireOp",EDGE,"E35.bottom"),sQuery(id+"F37.wireOp",EDGE,"E35.top"),sQuery(id+"F37.wireOp",EDGE,"E35.left"),sQuery(id+"F37.wireOp",EDGE,"E35.right"),sQuery(id+"F37.wireOp",EDGE,"E36.filletArc"),sQuery(id+"F37.wireOp",EDGE,"E37.filletArc"),sQuery(id+"F37.wireOp",EDGE,"E38.filletArc"),sQuery(id+"F37.wireOp",EDGE,"E39.filletArc")])]}),"instanceName":"1"});
            transform(context, id + "F40", {"entities" : qUnion([Q0, Q1]), "transformType" : TransformType.TRANSLATION_3D, "dx" : 0 * mm, "dy" : -970 * mm, "dz" : 0 * mm, "makeCopy" : true});
        }
        {
            var Q0;
            Q0=makeQuery(id+"F35.opPattern","COPY",FACE,{"derivedFrom":makeQuery(id+"F34.opPattern","COPY",FACE,{"derivedFrom":makeQuery(id+"F33.opExtrude","SWEPT_FACE",FACE,{"disambiguationData":[OSD([sQuery(id+"F32.wireOp",EDGE,"E28.top")])]}),"instanceName":"1"}),"instanceName":"1"});
            var sketch = newSketch(context, id + "F41", { "sketchPlane" : qUnion([Q0])});
            skLineSegment(sketch, "E40", {"start": v(440, -45) * mm, "end": v(440, 55) * mm});
            skLineSegment(sketch, "E41.bottom", {"start": v(453, 70) * mm, "end": v(427, 70) * mm});
            skLineSegment(sketch, "E41.top", {"start": v(453, 40) * mm, "end": v(427, 40) * mm});
            skLineSegment(sketch, "E41.left", {"start": v(455, 68) * mm, "end": v(455, 42) * mm});
            skLineSegment(sketch, "E41.right", {"start": v(425, 68) * mm, "end": v(425, 42) * mm});
            skPoint(sketch, "E41.middle", {"position": v(440, 55) * mm});
            skLineSegment(sketch, "E42.bottom", {"start": v(452, 67) * mm, "end": v(428, 67) * mm});
            skLineSegment(sketch, "E42.top", {"start": v(452, 43) * mm, "end": v(428, 43) * mm});
            skLineSegment(sketch, "E42.left", {"start": v(452, 67) * mm, "end": v(452, 43) * mm});
            skLineSegment(sketch, "E42.right", {"start": v(428, 67) * mm, "end": v(428, 43) * mm});
            skPoint(sketch, "E43.visualSharp", {"position": v(425, 70) * mm});
            skArc(sketch, "E43.filletArc", {"start": v(427, 70) * mm, "mid": v(425.59, 69.41) * mm, "end": v(425, 68) * mm});
            skPoint(sketch, "E44.visualSharp", {"position": v(455, 70) * mm});
            skArc(sketch, "E44.filletArc", {"start": v(455, 68) * mm, "mid": v(454.41, 69.41) * mm, "end": v(453, 70) * mm});
            skPoint(sketch, "E45.visualSharp", {"position": v(455, 40) * mm});
            skArc(sketch, "E45.filletArc", {"start": v(453, 40) * mm, "mid": v(454.41, 40.59) * mm, "end": v(455, 42) * mm});
            skPoint(sketch, "E46.visualSharp", {"position": v(425, 40) * mm});
            skArc(sketch, "E46.filletArc", {"start": v(425, 42) * mm, "mid": v(425.59, 40.59) * mm, "end": v(427, 40) * mm});
            skLineSegment(sketch, "E47.bottom", {"start": v(453, 780) * mm, "end": v(427, 780) * mm});
            skLineSegment(sketch, "E47.top", {"start": v(453, 810) * mm, "end": v(427, 810) * mm});
            skLineSegment(sketch, "E47.left", {"start": v(455, 782) * mm, "end": v(455, 808) * mm});
            skLineSegment(sketch, "E47.right", {"start": v(425, 782) * mm, "end": v(425, 808) * mm});
            skPoint(sketch, "E47.middle", {"position": v(440, 795) * mm});
            skLineSegment(sketch, "E48.bottom", {"start": v(452, 783) * mm, "end": v(428, 783) * mm});
            skLineSegment(sketch, "E48.top", {"start": v(452, 807) * mm, "end": v(428, 807) * mm});
            skLineSegment(sketch, "E48.left", {"start": v(452, 783) * mm, "end": v(452, 807) * mm});
            skLineSegment(sketch, "E48.right", {"start": v(428, 783) * mm, "end": v(428, 807) * mm});
            skPoint(sketch, "E49.visualSharp", {"position": v(425, 810) * mm});
            skArc(sketch, "E49.filletArc", {"start": v(427, 810) * mm, "mid": v(425.59, 809.41) * mm, "end": v(425, 808) * mm});
            skPoint(sketch, "E50.visualSharp", {"position": v(455, 810) * mm});
            skArc(sketch, "E50.filletArc", {"start": v(455, 808) * mm, "mid": v(454.41, 809.41) * mm, "end": v(453, 810) * mm});
            skPoint(sketch, "E51.visualSharp", {"position": v(455, 780) * mm});
            skArc(sketch, "E51.filletArc", {"start": v(453, 780) * mm, "mid": v(454.41, 780.59) * mm, "end": v(455, 782) * mm});
            skPoint(sketch, "E52.visualSharp", {"position": v(425, 780) * mm});
            skArc(sketch, "E52.filletArc", {"start": v(425, 782) * mm, "mid": v(425.59, 780.59) * mm, "end": v(427, 780) * mm});
            skSolve(sketch);
        }
        {
            var Q0;
            {var subQ10=sQuery(id+"F41.wireOp",EDGE,"E41.bottom");Q0=makeQuery(id+"F41.imprint","IMPRINT",FACE,{"disambiguationData":[TD([[makeQuery(id+"F41.imprint","IMPRINT",EDGE,{"derivedFrom":subQ10}),1.0]])]});}
            var Q1;
            Q1=makeQuery(id+"F41.imprint","IMPRINT",FACE,{"disambiguationData":[TD([[makeQuery(id+"F41.imprint","IMPRINT",EDGE,{"derivedFrom":sQuery(id+"F41.wireOp",EDGE,"E41.left")}),-1.0]])]});
            var Q2;
            Q2=makeQuery(id+"F41.imprint","IMPRINT",FACE,{"disambiguationData":[TD([[makeQuery(id+"F41.imprint","IMPRINT",EDGE,{"derivedFrom":sQuery(id+"F41.wireOp",EDGE,"E41.right")}),1.0]])]});
            extrude(context, id + "F42", {"entities" : qUnion([Q0, Q1, Q2]), "operationType" : NewBodyOperationType.ADD, "depth" : 100 * mm});
        }
        {
            var Q0;
            Q0=makeQuery(id+"F41.imprint","IMPRINT",FACE,{"disambiguationData":[TD([[makeQuery(id+"F41.imprint","IMPRINT",EDGE,{"derivedFrom":sQuery(id+"F41.wireOp",EDGE,"E47.right")}),-1.0]])]});
            var Q1;
            Q1=makeQuery(id+"F41.imprint","IMPRINT",FACE,{"disambiguationData":[TD([[makeQuery(id+"F41.imprint","IMPRINT",EDGE,{"derivedFrom":sQuery(id+"F41.wireOp",EDGE,"E47.left")}),1.0]])]});
            var Q2;
            {var subQ0=sQuery(id+"F41.wireOp",EDGE,"E47.bottom");Q2=makeQuery(id+"F41.imprint","IMPRINT",FACE,{"disambiguationData":[TD([[makeQuery(id+"F41.imprint","IMPRINT",EDGE,{"derivedFrom":subQ0}),-1.0]])]});}
            extrude(context, id + "F43", {"entities" : qUnion([Q0, Q1, Q2]), "operationType" : NewBodyOperationType.ADD, "depth" : 100 * mm});
        }
        {
            var Q0;
            Q0=makeQuery(id+"F42.opExtrude","SWEPT_FACE",FACE,{"disambiguationData":[OSD([sQuery(id+"F41.wireOp",EDGE,"E41.left")])]});
            var sketch = newSketch(context, id + "F44", { "sketchPlane" : qUnion([Q0])});
            skLineSegment(sketch, "E53", {"start": v(55, 450.24) * mm, "end": v(55, 435.24) * mm});
            skLineSegment(sketch, "E54.bottom", {"start": v(68, 420.24) * mm, "end": v(40, 420.24) * mm});
            skLineSegment(sketch, "E54.top", {"start": v(68, 450.24) * mm, "end": v(42, 450.24) * mm});
            skLineSegment(sketch, "E54.left", {"start": v(70, 422.24) * mm, "end": v(70, 448.24) * mm});
            skLineSegment(sketch, "E54.right", {"start": v(40, 420.24) * mm, "end": v(40, 448.24) * mm});
            skPoint(sketch, "E54.middle", {"position": v(55, 435.24) * mm});
            skLineSegment(sketch, "E55.bottom", {"start": v(67, 423.24) * mm, "end": v(43, 423.24) * mm});
            skLineSegment(sketch, "E55.top", {"start": v(67, 447.24) * mm, "end": v(43, 447.24) * mm});
            skLineSegment(sketch, "E55.left", {"start": v(67, 423.24) * mm, "end": v(67, 447.24) * mm});
            skLineSegment(sketch, "E55.right", {"start": v(43, 423.24) * mm, "end": v(43, 447.24) * mm});
            skPoint(sketch, "E56.visualSharp", {"position": v(70, 450.24) * mm});
            skArc(sketch, "E56.filletArc", {"start": v(70, 448.24) * mm, "mid": v(69.41, 449.66) * mm, "end": v(68, 450.24) * mm});
            skPoint(sketch, "E57.visualSharp", {"position": v(70, 420.24) * mm});
            skArc(sketch, "E57.filletArc", {"start": v(68, 420.24) * mm, "mid": v(69.41, 420.83) * mm, "end": v(70, 422.24) * mm});
            skPoint(sketch, "E58.visualSharp", {"position": v(40, 450.24) * mm});
            skArc(sketch, "E58.filletArc", {"start": v(42, 450.24) * mm, "mid": v(40.59, 449.66) * mm, "end": v(40, 448.24) * mm});
            skSolve(sketch);
        }
        {
            var Q0;
            Q0=makeQuery(id+"F44.imprint","IMPRINT",FACE,{"disambiguationData":[TD([[makeQuery(id+"F44.imprint","IMPRINT",EDGE,{"derivedFrom":sQuery(id+"F44.wireOp",EDGE,"E54.left")}),1.0]])]});
            var Q1;
            Q1=makeQuery(id+"F44.imprint","IMPRINT",FACE,{"disambiguationData":[TD([[makeQuery(id+"F44.imprint","IMPRINT",EDGE,{"derivedFrom":sQuery(id+"F44.wireOp",EDGE,"E55.bottom")}),1.0]])]});
            var Q2;
            {var subQ0=sQuery(id+"F44.wireOp",EDGE,"E54.right");Q2=makeQuery(id+"F44.imprint","IMPRINT",FACE,{"disambiguationData":[TD([[makeQuery(id+"F44.imprint","IMPRINT",EDGE,{"derivedFrom":subQ0}),-1.0]])]});}
            extrude(context, id + "F45", {"entities" : qUnion([Q0, Q1, Q2]), "operationType" : NewBodyOperationType.ADD, "depth" : 250 * mm});
        }
        {
            var Q0;
            Q0=makeQuery(id+"F43.opExtrude","SWEPT_FACE",FACE,{"disambiguationData":[OSD([sQuery(id+"F41.wireOp",EDGE,"E47.left")])]});
            var sketch = newSketch(context, id + "F46", { "sketchPlane" : qUnion([Q0])});
            skLineSegment(sketch, "E59", {"start": v(795, 450.24) * mm, "end": v(795, 435.24) * mm});
            skLineSegment(sketch, "E60.bottom", {"start": v(808, 420.24) * mm, "end": v(782, 420.24) * mm});
            skLineSegment(sketch, "E60.top", {"start": v(808, 450.24) * mm, "end": v(782, 450.24) * mm});
            skLineSegment(sketch, "E60.left", {"start": v(810, 422.24) * mm, "end": v(810, 448.24) * mm});
            skLineSegment(sketch, "E60.right", {"start": v(780, 422.24) * mm, "end": v(780, 448.24) * mm});
            skPoint(sketch, "E60.middle", {"position": v(795, 435.24) * mm});
            skPoint(sketch, "E61.visualSharp", {"position": v(780, 420.24) * mm});
            skArc(sketch, "E61.filletArc", {"start": v(780, 422.24) * mm, "mid": v(780.59, 420.83) * mm, "end": v(782, 420.24) * mm});
            skPoint(sketch, "E62.visualSharp", {"position": v(780, 450.24) * mm});
            skArc(sketch, "E62.filletArc", {"start": v(782, 450.24) * mm, "mid": v(780.59, 449.66) * mm, "end": v(780, 448.24) * mm});
            skPoint(sketch, "E63.visualSharp", {"position": v(810, 450.24) * mm});
            skArc(sketch, "E63.filletArc", {"start": v(810, 448.24) * mm, "mid": v(809.41, 449.66) * mm, "end": v(808, 450.24) * mm});
            skPoint(sketch, "E64.visualSharp", {"position": v(810, 420.24) * mm});
            skArc(sketch, "E64.filletArc", {"start": v(808, 420.24) * mm, "mid": v(809.41, 420.83) * mm, "end": v(810, 422.24) * mm});
            skLineSegment(sketch, "E65.bottom", {"start": v(807, 423.24) * mm, "end": v(783, 423.24) * mm});
            skLineSegment(sketch, "E65.top", {"start": v(807, 447.24) * mm, "end": v(783, 447.24) * mm});
            skLineSegment(sketch, "E65.left", {"start": v(807, 423.24) * mm, "end": v(807, 447.24) * mm});
            skLineSegment(sketch, "E65.right", {"start": v(783, 423.24) * mm, "end": v(783, 447.24) * mm});
            skSolve(sketch);
        }
        {
            var Q0;
            Q0=makeQuery(id+"F46.imprint","IMPRINT",FACE,{"disambiguationData":[TD([[makeQuery(id+"F46.imprint","IMPRINT",EDGE,{"derivedFrom":sQuery(id+"F46.wireOp",EDGE,"E60.right")}),-1.0]])]});
            var Q1;
            Q1=makeQuery(id+"F46.imprint","IMPRINT",FACE,{"disambiguationData":[TD([[makeQuery(id+"F46.imprint","IMPRINT",EDGE,{"derivedFrom":sQuery(id+"F46.wireOp",EDGE,"E60.left")}),1.0]])]});
            var Q2;
            {var subQ8=sQuery(id+"F46.wireOp",EDGE,"E60.bottom");Q2=makeQuery(id+"F46.imprint","IMPRINT",FACE,{"disambiguationData":[TD([[makeQuery(id+"F46.imprint","IMPRINT",EDGE,{"derivedFrom":subQ8}),-1.0]])]});}
            extrude(context, id + "F47", {"entities" : qUnion([Q0, Q1, Q2]), "operationType" : NewBodyOperationType.ADD, "depth" : 250 * mm});
        }
        {
            var Q0;
            Q0=makeQuery(id+"F40.opPattern","COPY",FACE,{"derivedFrom":makeQuery(id+"F39.opPattern","COPY",FACE,{"derivedFrom":makeQuery(id+"F38.opExtrude","SWEPT_FACE",FACE,{"disambiguationData":[OSD([sQuery(id+"F37.wireOp",EDGE,"E34.right")])]}),"instanceName":"1"}),"instanceName":"1"});
            var sketch = newSketch(context, id + "F48", { "sketchPlane" : qUnion([Q0])});
            skLineSegment(sketch, "E66", {"start": v(220, 348) * mm, "end": v(220, 548) * mm});
            skCircle(sketch, "E67", {"center": v(220, 548) * mm, "radius": 200 * mm});
            skCircle(sketch, "E68", {"center": v(220, 548) * mm, "radius": 195 * mm});
            skSolve(sketch);
        }
        {
            var Q0;
            Q0=makeQuery(id+"F48.imprint","IMPRINT",FACE,{"disambiguationData":[TD([[makeQuery(id+"F48.imprint","IMPRINT",EDGE,{"derivedFrom":sQuery(id+"F48.wireOp",EDGE,"E67")}),1.0]])]});
            extrude(context, id + "F49", {"entities" : qUnion([Q0]), "oppositeDirection" : true, "depth" : 1000 * mm});
        }
        {
            var Q0;
            Q0=makeQuery(id+"F49.opExtrude","CAP_FACE",FACE,{"disambiguationData":[OSD([sQuery(id+"F48.wireOp",EDGE,"E67"),sQuery(id+"F48.wireOp",EDGE,"E68")])],"isStart":true});
            extrude(context, id + "F50", {"entities" : qUnion([Q0]), "operationType" : NewBodyOperationType.ADD, "depth" : 100 * mm});
        }
        {
            var Q0;
            Q0=makeQuery(id+"F50.opExtrude","CAP_FACE",FACE,{"disambiguationData":[OSD([sQuery(id+"F48.wireOp",EDGE,"E67"),sQuery(id+"F48.wireOp",EDGE,"E68")])],"isStart":false});
            var sketch = newSketch(context, id + "F51", { "sketchPlane" : qUnion([Q0])});
            skLineSegment(sketch, "E69", {"start": v(229.88, 348.24) * mm, "end": v(220, 548) * mm});
            skCircle(sketch, "E70", {"center": v(220, 548) * mm, "radius": 195 * mm});
            skSolve(sketch);
        }
        {
            var Q0;
            Q0=makeQuery(id+"F51.imprint","IMPRINT",FACE,{"disambiguationData":[TD([[makeQuery(id+"F51.imprint","IMPRINT",EDGE,{"derivedFrom":sQuery(id+"F51.wireOp",EDGE,"E70")}),1.0]])]});
            extrude(context, id + "F52", {"entities" : qUnion([Q0]), "operationType" : NewBodyOperationType.ADD, "oppositeDirection" : true, "depth" : 5 * mm});
        }
        {
            var Q0;
            Q0=makeQuery(id+"F49.opExtrude","CAP_FACE",FACE,{"disambiguationData":[OSD([sQuery(id+"F48.wireOp",EDGE,"E67"),sQuery(id+"F48.wireOp",EDGE,"E68")])],"isStart":false});
            var sketch = newSketch(context, id + "F53", { "sketchPlane" : qUnion([Q0])});
            skCircle(sketch, "E71", {"center": v(-220, 548) * mm, "radius": 195 * mm});
            skSolve(sketch);
        }
        {
            var Q0;
            Q0=makeQuery(id+"F53.imprint","IMPRINT",FACE,{"disambiguationData":[TD([[makeQuery(id+"F53.imprint","IMPRINT",EDGE,{"derivedFrom":sQuery(id+"F53.wireOp",EDGE,"E71")}),-1.0]])]});
            extrude(context, id + "F54", {"entities" : qUnion([Q0]), "operationType" : NewBodyOperationType.ADD, "oppositeDirection" : true, "depth" : 5 * mm});
        }
        {
            var Q0;
            Q0=makeQuery(id+"F54.boolean.opBoolean","MERGE",FACE,{"derivedFrom":[makeQuery(id+"F49.opExtrude","CAP_FACE",FACE,{"disambiguationData":[OSD([sQuery(id+"F48.wireOp",EDGE,"E67"),sQuery(id+"F48.wireOp",EDGE,"E68")])],"isStart":false}),makeQuery(id+"F54.opExtrude","CAP_FACE",FACE,{"disambiguationData":[OSD([sQuery(id+"F53.wireOp",EDGE,"E71")])],"isStart":true})]});
            var sketch = newSketch(context, id + "F55", { "sketchPlane" : qUnion([Q0])});
            skCircle(sketch, "E72", {"center": v(-220, 281) * mm, "radius": 200 * mm});
            skSolve(sketch);
        }
        {
            var Q0;
            {var subQ0=sQuery(id+"F55.wireOp",EDGE,"E72");var subQ1=makeQuery(id+"F49.opExtrude","CAP_EDGE",EDGE,{"disambiguationData":[OSD([sQuery(id+"F48.wireOp",EDGE,"E67")])],"isStart":false});var subQ2=makeQuery(id+"F55.imprint","INTERSECT",VERTEX,{"disambiguationData":[OD(0.0)],"derivedFrom":[subQ1,subQ0]});Q0=makeQuery(id+"F55.imprint","IMPRINT",FACE,{"disambiguationData":[TD([[makeQuery(id+"F55.imprint","IMPRINT",EDGE,{"disambiguationData":[TD([[subQ2,-1.0]])],"derivedFrom":subQ0}),1.0]])]});}
            var Q1;
            {var subQ0=sQuery(id+"F55.wireOp",EDGE,"E72");var subQ1=makeQuery(id+"F49.opExtrude","CAP_EDGE",EDGE,{"disambiguationData":[OSD([sQuery(id+"F48.wireOp",EDGE,"E67")])],"isStart":false});var subQ2=makeQuery(id+"F55.imprint","INTERSECT",VERTEX,{"disambiguationData":[OD(0.0)],"derivedFrom":[subQ1,subQ0]});Q1=makeQuery(id+"F55.imprint","IMPRINT",FACE,{"disambiguationData":[TD([[makeQuery(id+"F55.imprint","IMPRINT",EDGE,{"disambiguationData":[TD([[subQ2,1.0]])],"derivedFrom":subQ0}),1.0]])]});}
            extrude(context, id + "F56", {"entities" : qUnion([Q0, Q1]), "depth" : 500 * mm});
        }
        {
            var Q0;
            Q0=makeQuery(id+"F40.opPattern","COPY",FACE,{"derivedFrom":makeQuery(id+"F39.opPattern","COPY",FACE,{"derivedFrom":makeQuery(id+"F38.opExtrude","SWEPT_FACE",FACE,{"disambiguationData":[OSD([sQuery(id+"F37.wireOp",EDGE,"E34.right")])]}),"instanceName":"1"}),"instanceName":"1"});
            var sketch = newSketch(context, id + "F57", { "sketchPlane" : qUnion([Q0])});
            skLineSegment(sketch, "E73.left", {"start": v(330, 380.97) * mm, "end": v(330, 322) * mm});
            skLineSegment(sketch, "E73.right", {"start": v(110, 380.97) * mm, "end": v(110, 322) * mm});
            skPoint(sketch, "E73.middle", {"position": v(220, 348) * mm});
            skCircle(sketch, "E74", {"center": v(220, 548) * mm, "radius": 200 * mm});
            skPoint(sketch, "E75.orphan", {"position": v(330, 398) * mm});
            skPoint(sketch, "E73.bottom.end.orphan", {"position": v(110, 398) * mm});
            skLineSegment(sketch, "E76", {"start": v(110, 322) * mm, "end": v(330, 322) * mm});
            skSolve(sketch);
        }
        {
            var Q0;
            {var subQ0=sQuery(id+"F57.wireOp",EDGE,"E74");var subQ1=sQuery(id+"F57.wireOp",EDGE,"E73.right");var subQ2=makeQuery(id+"F57.imprint","INTERSECT",VERTEX,{"derivedFrom":[subQ1,subQ0]});Q0=makeQuery(id+"F57.imprint","IMPRINT",FACE,{"disambiguationData":[TD([[makeQuery(id+"F57.imprint","IMPRINT",EDGE,{"disambiguationData":[TD([[subQ2,-1.0]])],"derivedFrom":subQ1}),1.0]])]});}
            var Q1;
            {var subQ0=sQuery(id+"F57.wireOp",EDGE,"E74");var subQ1=sQuery(id+"F57.wireOp",EDGE,"E73.left");var subQ2=makeQuery(id+"F57.imprint","INTERSECT",VERTEX,{"derivedFrom":[subQ1,subQ0]});Q1=makeQuery(id+"F57.imprint","IMPRINT",FACE,{"disambiguationData":[TD([[makeQuery(id+"F57.imprint","IMPRINT",EDGE,{"disambiguationData":[TD([[subQ2,-1.0]])],"derivedFrom":subQ1}),-1.0]])]});}
            var Q2;
            {var subQ0=sQuery(id+"F57.wireOp",EDGE,"E76");Q2=makeQuery(id+"F57.imprint","IMPRINT",FACE,{"disambiguationData":[TD([[makeQuery(id+"F57.imprint","IMPRINT",EDGE,{"derivedFrom":subQ0}),-1.0]])]});}
            extrude(context, id + "F58", {"entities" : qUnion([Q0, Q1, Q2]), "depth" : 5 * mm});
        }
        {
            var Q0;
            Q0=makeQuery(id+"F58.opExtrude","SWEPT_BODY",BODY,{"disambiguationData":[OSD([sQuery(id+"F57.wireOp",EDGE,"E73.left"),sQuery(id+"F57.wireOp",EDGE,"E73.right"),sQuery(id+"F57.wireOp",EDGE,"E74"),sQuery(id+"F57.wireOp",EDGE,"E76")])]});
            transform(context, id + "F59", {"entities" : qUnion([Q0]), "transformType" : TransformType.TRANSLATION_3D, "dx" : 0 * mm, "dy" : 35 * mm, "dz" : 0 * mm, "makeCopy" : false});
        }
        {
            var Q0;
            Q0=makeQuery(id+"F58.opExtrude","SWEPT_BODY",BODY,{"disambiguationData":[OSD([sQuery(id+"F57.wireOp",EDGE,"E73.left"),sQuery(id+"F57.wireOp",EDGE,"E73.right"),sQuery(id+"F57.wireOp",EDGE,"E74"),sQuery(id+"F57.wireOp",EDGE,"E76")])]});
            transform(context, id + "F60", {"entities" : qUnion([Q0]), "transformType" : TransformType.TRANSLATION_3D, "dx" : 0 * mm, "dy" : 935 * mm, "dz" : 0 * mm, "makeCopy" : true});
        }
    });
